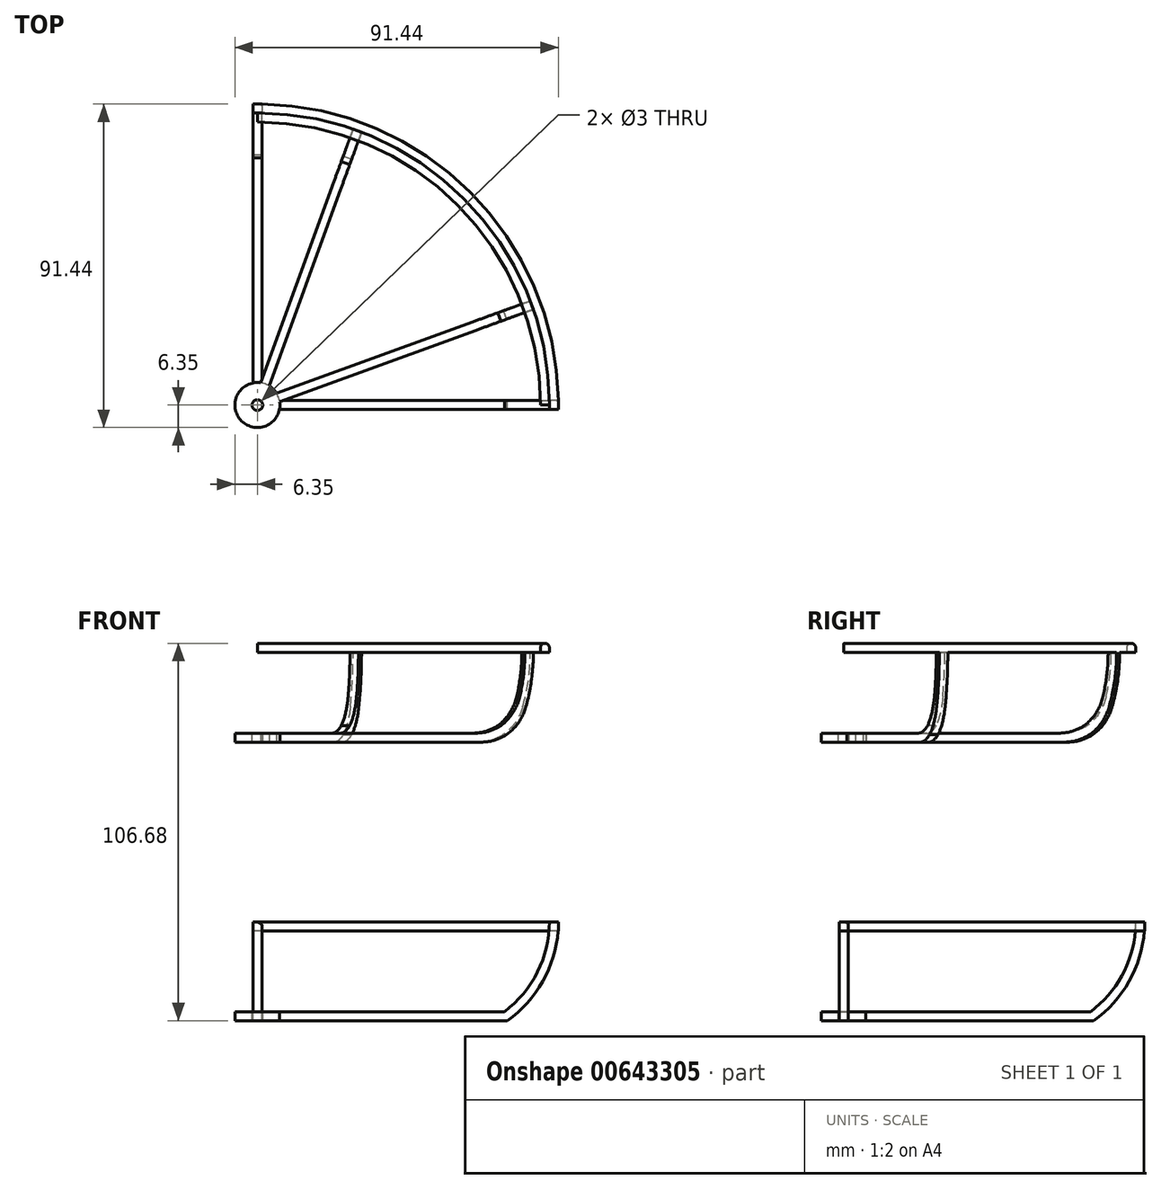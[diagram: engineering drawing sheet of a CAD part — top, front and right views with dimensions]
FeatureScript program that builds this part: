
annotation { "Feature Type Name" : "Feature", "Feature Type Description" : "" }
export const myFeature = defineFeature(function(context is Context, id is Id, definition is map)
    precondition{}
    {
        {
            var Q0;
            Q0=qCreatedBy(makeId("Front.planeOp"),FACE);
            var sketch = newSketch(context, id + "F0", { "sketchPlane" : qUnion([Q0])});
            skLineSegment(sketch, "E0", {"start": v(0, 0) * mm, "end": v(69.85, 0) * mm});
            skLineSegment(sketch, "E1.bottom", {"start": v(69.85, 0) * mm, "end": v(82.55, 0) * mm, "construction": true});
            skLineSegment(sketch, "E1.top", {"start": v(69.85, 25.4) * mm, "end": v(82.55, 25.4) * mm, "construction": true});
            skLineSegment(sketch, "E1.left", {"start": v(69.85, 0) * mm, "end": v(69.85, 25.4) * mm, "construction": true});
            skLineSegment(sketch, "E1.right", {"start": v(82.55, 0) * mm, "end": v(82.55, 25.4) * mm, "construction": true});
            skArc(sketch, "E2", {"start": v(69.85, 0) * mm, "mid": v(79.2, 11.2) * mm, "end": v(82.55, 25.4) * mm});
            skArc(sketch, "E3.0", {"start": v(70.68, -2.54) * mm, "mid": v(81.27, 9.68) * mm, "end": v(85.1, 25.4) * mm});
            skLineSegment(sketch, "E3.1", {"start": v(0, -2.54) * mm, "end": v(70.68, -2.54) * mm});
            skLineSegment(sketch, "E4", {"start": v(82.55, 25.4) * mm, "end": v(85.1, 25.4) * mm});
            skLineSegment(sketch, "E5", {"start": v(0, 0) * mm, "end": v(0, -2.54) * mm});
            skSolve(sketch);
        }
        {
            var Q0;
            Q0 = qSketchRegion(id + "F0", true);
            extrude(context, id + "F1", {"entities" : qUnion([Q0]), "depth" : 2.54 * mm, "offsetDistance" : 25.4 * mm, "symmetric" : true});
        }
        {
            var Q0;
            Q0=qCreatedBy(makeId("Right.planeOp"),FACE);
            var sketch = newSketch(context, id + "F2", { "sketchPlane" : qUnion([Q0])});
            skLineSegment(sketch, "E6", {"start": v(0, 0) * mm, "end": v(69.85, 0) * mm});
            skLineSegment(sketch, "E7.bottom", {"start": v(69.85, 0) * mm, "end": v(82.55, 0) * mm, "construction": true});
            skLineSegment(sketch, "E7.top", {"start": v(69.85, 25.4) * mm, "end": v(82.55, 25.4) * mm, "construction": true});
            skLineSegment(sketch, "E7.left", {"start": v(69.85, 0) * mm, "end": v(69.85, 25.4) * mm, "construction": true});
            skLineSegment(sketch, "E7.right", {"start": v(82.55, 0) * mm, "end": v(82.55, 25.4) * mm, "construction": true});
            skArc(sketch, "E8", {"start": v(69.85, 0) * mm, "mid": v(79.2, 11.2) * mm, "end": v(82.55, 25.4) * mm});
            skArc(sketch, "E9.0", {"start": v(70.68, -2.54) * mm, "mid": v(81.27, 9.68) * mm, "end": v(85.1, 25.4) * mm});
            skLineSegment(sketch, "E9.1", {"start": v(0, -2.54) * mm, "end": v(70.68, -2.54) * mm});
            skLineSegment(sketch, "E10", {"start": v(82.55, 25.4) * mm, "end": v(85.1, 25.4) * mm});
            skLineSegment(sketch, "E11", {"start": v(0, 0) * mm, "end": v(0, -2.54) * mm});
            skSolve(sketch);
        }
        {
            var Q0;
            Q0 = qSketchRegion(id + "F2", true);
            extrude(context, id + "F3", {"entities" : qUnion([Q0]), "operationType" : NewBodyOperationType.ADD, "depth" : 2.54 * mm, "offsetDistance" : 25.4 * mm, "symmetric" : true});
        }
        {
            var Q0;
            Q0=makeQuery(id+"F3.opExtrude","SWEPT_FACE",FACE,{"disambiguationData":[OSD([sQuery(id+"F2.wireOp",EDGE,"E10")])]});
            var sketch = newSketch(context, id + "F4", { "sketchPlane" : qUnion([Q0])});
            skPoint(sketch, "E12", {"position": v(0, 82.55) * mm});
            skLineSegment(sketch, "E13.bottom", {"start": v(0, 82.55) * mm, "end": v(82.55, 82.55) * mm, "construction": true});
            skLineSegment(sketch, "E13.top", {"start": v(0, 0) * mm, "end": v(82.55, 0) * mm, "construction": true});
            skLineSegment(sketch, "E13.left", {"start": v(0, 82.55) * mm, "end": v(0, 0) * mm, "construction": true});
            skLineSegment(sketch, "E13.right", {"start": v(82.55, 82.55) * mm, "end": v(82.55, 0) * mm, "construction": true});
            skArc(sketch, "E14", {"start": v(82.55, 0) * mm, "mid": v(58.37, 58.37) * mm, "end": v(0, 82.55) * mm});
            skArc(sketch, "E15.0", {"start": v(85.1, 0) * mm, "mid": v(60.17, 60.17) * mm, "end": v(0, 85.1) * mm});
            skLineSegment(sketch, "E16", {"start": v(82.55, 0) * mm, "end": v(83.82, 0) * mm, "construction": true});
            skLineSegment(sketch, "E17.bottom", {"start": v(85.1, -1.27) * mm, "end": v(82.55, -1.27) * mm});
            skLineSegment(sketch, "E17.top", {"start": v(85.1, 1.27) * mm, "end": v(82.55, 1.27) * mm});
            skLineSegment(sketch, "E17.left", {"start": v(85.1, -1.27) * mm, "end": v(85.1, 1.27) * mm});
            skLineSegment(sketch, "E17.right", {"start": v(82.55, -1.27) * mm, "end": v(82.55, 1.27) * mm});
            skPoint(sketch, "E17.middle", {"position": v(83.82, 0) * mm});
            skLineSegment(sketch, "E18", {"start": v(0, 82.55) * mm, "end": v(0, 83.82) * mm, "construction": true});
            skLineSegment(sketch, "E19.bottom", {"start": v(1.27, 85.1) * mm, "end": v(-1.27, 85.1) * mm});
            skLineSegment(sketch, "E19.top", {"start": v(1.27, 82.55) * mm, "end": v(-1.27, 82.55) * mm});
            skLineSegment(sketch, "E19.left", {"start": v(1.27, 85.1) * mm, "end": v(1.27, 82.55) * mm});
            skLineSegment(sketch, "E19.right", {"start": v(-1.27, 85.1) * mm, "end": v(-1.27, 82.55) * mm});
            skPoint(sketch, "E19.middle", {"position": v(0, 83.82) * mm});
            skSolve(sketch);
        }
        {
            var Q0;
            Q0 = qSketchRegion(id + "F4", true);
            extrude(context, id + "F5", {"entities" : qUnion([Q0]), "operationType" : NewBodyOperationType.ADD, "oppositeDirection" : true, "depth" : 2.54 * mm, "offsetDistance" : 25.4 * mm});
        }
        {
            var Q0;
            Q0=qCreatedBy(makeId("Top.planeOp"),FACE);
            var sketch = newSketch(context, id + "F6", { "sketchPlane" : qUnion([Q0])});
            skCircle(sketch, "E20", {"center": v(0, 0) * mm, "radius": 6.35 * mm});
            skSolve(sketch);
        }
        {
            var Q0;
            Q0 = qSketchRegion(id + "F6", true);
            extrude(context, id + "F7", {"entities" : qUnion([Q0]), "operationType" : NewBodyOperationType.ADD, "oppositeDirection" : true, "depth" : 2.54 * mm, "offsetDistance" : 25.4 * mm});
        }
        {
            var Q0;
            Q0=qCreatedBy(makeId("Top.planeOp"),FACE);
            var sketch = newSketch(context, id + "F8", { "sketchPlane" : qUnion([Q0])});
            skCircle(sketch, "E21", {"center": v(0, 0) * mm, "radius": 1.5 * mm});
            skSolve(sketch);
        }
        {
            var Q0;
            Q0 = qSketchRegion(id + "F8", true);
            extrude(context, id + "F9", {"entities" : qUnion([Q0]), "operationType" : NewBodyOperationType.REMOVE, "oppositeDirection" : true, "depth" : 2.54 * mm, "offsetDistance" : 25.4 * mm});
        }
        {
            var Q0;
            Q0=makeQuery(id+"F5.boolean.opBoolean","MERGE",FACE,{"derivedFrom":[makeQuery(id+"F1.opExtrude","SWEPT_FACE",FACE,{"disambiguationData":[OSD([sQuery(id+"F0.wireOp",EDGE,"E4")])]}),makeQuery(id+"F3.opExtrude","SWEPT_FACE",FACE,{"disambiguationData":[OSD([sQuery(id+"F2.wireOp",EDGE,"E10")])]}),makeQuery(id+"F5.opExtrude","CAP_FACE",FACE,{"disambiguationData":[OSD([sQuery(id+"F4.wireOp",EDGE,"E14"),sQuery(id+"F4.wireOp",EDGE,"E15.0"),sQuery(id+"F4.wireOp",EDGE,"E17.bottom"),sQuery(id+"F4.wireOp",EDGE,"E17.top"),sQuery(id+"F4.wireOp",EDGE,"E17.left"),sQuery(id+"F4.wireOp",EDGE,"E17.right"),sQuery(id+"F4.wireOp",EDGE,"E19.bottom"),sQuery(id+"F4.wireOp",EDGE,"E19.top"),sQuery(id+"F4.wireOp",EDGE,"E19.left"),sQuery(id+"F4.wireOp",EDGE,"E19.right")])],"isStart":true})]});
            cPlane(context, id + "F10", {"entities" : qUnion([Q0]), "cplaneType" : CPlaneType.OFFSET, "offset" : 50.8 * mm, "width" : 152.4 * mm, "height" : 152.4 * mm});
        }
        {
            var Q0;
            Q0=qCreatedBy(id+"F10.planeOp",FACE);
            var sketch = newSketch(context, id + "F11", { "sketchPlane" : qUnion([Q0])});
            skCircle(sketch, "E22", {"center": v(0, 0) * mm, "radius": 6.35 * mm});
            skLineSegment(sketch, "E23", {"start": v(0, 0) * mm, "end": v(69.85, 0) * mm, "construction": true});
            skLineSegment(sketch, "E24", {"start": v(0, 0) * mm, "end": v(71.6, 26.06) * mm, "construction": true});
            skLineSegment(sketch, "E25", {"start": v(0, 0) * mm, "end": v(26.06, 71.6) * mm, "construction": true});
            skLineSegment(sketch, "E26.0", {"start": v(-2.12, -2.12) * mm, "end": v(72.04, 24.87) * mm});
            skLineSegment(sketch, "E26.1", {"start": v(-2.12, -2.12) * mm, "end": v(24.87, 72.04) * mm});
            skLineSegment(sketch, "E27.0", {"start": v(2.12, 2.12) * mm, "end": v(71.17, 27.26) * mm});
            skLineSegment(sketch, "E27.1", {"start": v(2.12, 2.12) * mm, "end": v(27.26, 71.17) * mm});
            skLineSegment(sketch, "E28", {"start": v(24.87, 72.04) * mm, "end": v(27.26, 71.17) * mm});
            skLineSegment(sketch, "E29", {"start": v(71.17, 27.26) * mm, "end": v(72.04, 24.87) * mm});
            skSolve(sketch);
        }
        {
            var Q0;
            Q0 = qSketchRegion(id + "F11", true);
            extrude(context, id + "F12", {"entities" : qUnion([Q0]), "depth" : 2.54 * mm, "offsetDistance" : 25.4 * mm});
        }
        {
            var Q0;
            Q0=makeQuery(id+"F12.opExtrude","SWEPT_FACE",FACE,{"disambiguationData":[OSD([sQuery(id+"F11.wireOp",EDGE,"E26.0")])]});
            var sketch = newSketch(context, id + "F13", { "sketchPlane" : qUnion([Q0])});
            skLineSegment(sketch, "E30.bottom", {"start": v(76.2, 76.2) * mm, "end": v(82.55, 76.2) * mm, "construction": true});
            skLineSegment(sketch, "E30.top", {"start": v(76.2, 101.6) * mm, "end": v(82.55, 101.6) * mm, "construction": true});
            skLineSegment(sketch, "E30.left", {"start": v(76.2, 76.2) * mm, "end": v(76.2, 101.6) * mm, "construction": true});
            skLineSegment(sketch, "E30.right", {"start": v(82.55, 76.2) * mm, "end": v(82.55, 101.6) * mm, "construction": true});
            skArc(sketch, "E31", {"start": v(76.2, 76.2) * mm, "mid": v(80.94, 88.5) * mm, "end": v(82.55, 101.6) * mm});
            skArc(sketch, "E32.0", {"start": v(73.96, 77.4) * mm, "mid": v(78.47, 89.13) * mm, "end": v(80.01, 101.6) * mm});
            skLineSegment(sketch, "E33", {"start": v(73.96, 77.4) * mm, "end": v(76.2, 76.2) * mm});
            skLineSegment(sketch, "E34", {"start": v(82.55, 101.6) * mm, "end": v(80.01, 101.6) * mm});
            skSolve(sketch);
        }
        {
            var Q0;
            Q0 = qSketchRegion(id + "F13", true);
            extrude(context, id + "F14", {"entities" : qUnion([Q0]), "operationType" : NewBodyOperationType.ADD, "oppositeDirection" : true, "depth" : 2.54 * mm, "offsetDistance" : 25.4 * mm});
        }
        {
            var Q0;
            Q0=makeQuery(id+"F12.opExtrude","SWEPT_FACE",FACE,{"disambiguationData":[OSD([sQuery(id+"F11.wireOp",EDGE,"E27.1")])]});
            var sketch = newSketch(context, id + "F15", { "sketchPlane" : qUnion([Q0])});
            skLineSegment(sketch, "E35.bottom", {"start": v(76.2, 76.2) * mm, "end": v(82.55, 76.2) * mm, "construction": true});
            skLineSegment(sketch, "E35.top", {"start": v(76.2, 101.6) * mm, "end": v(82.55, 101.6) * mm, "construction": true});
            skLineSegment(sketch, "E35.left", {"start": v(76.2, 76.2) * mm, "end": v(76.2, 101.6) * mm, "construction": true});
            skLineSegment(sketch, "E35.right", {"start": v(82.55, 76.2) * mm, "end": v(82.55, 101.6) * mm, "construction": true});
            skArc(sketch, "E36", {"start": v(76.2, 76.2) * mm, "mid": v(80.94, 88.5) * mm, "end": v(82.55, 101.6) * mm});
            skArc(sketch, "E37.0", {"start": v(73.96, 77.4) * mm, "mid": v(78.47, 89.13) * mm, "end": v(80.01, 101.6) * mm});
            skLineSegment(sketch, "E38", {"start": v(73.96, 77.4) * mm, "end": v(76.2, 76.2) * mm});
            skLineSegment(sketch, "E39", {"start": v(82.55, 101.6) * mm, "end": v(80.01, 101.6) * mm});
            skSolve(sketch);
        }
        {
            var Q0;
            Q0 = qSketchRegion(id + "F15", true);
            extrude(context, id + "F16", {"entities" : qUnion([Q0]), "operationType" : NewBodyOperationType.ADD, "oppositeDirection" : true, "depth" : 2.54 * mm, "offsetDistance" : 25.4 * mm});
        }
        {
            var Q0;
            Q0=makeQuery(id+"F16.opExtrude","SWEPT_FACE",FACE,{"disambiguationData":[OSD([sQuery(id+"F15.wireOp",EDGE,"E39")])]});
            var sketch = newSketch(context, id + "F17", { "sketchPlane" : qUnion([Q0])});
            skLineSegment(sketch, "E40", {"start": v(0, 0) * mm, "end": v(0, 80.01) * mm, "construction": true});
            skLineSegment(sketch, "E41", {"start": v(0, 0) * mm, "end": v(80.01, 0) * mm, "construction": true});
            skArc(sketch, "E42", {"start": v(80.01, 0) * mm, "mid": v(56.58, 56.58) * mm, "end": v(0, 80.01) * mm});
            skArc(sketch, "E43.0", {"start": v(82.55, 0) * mm, "mid": v(58.37, 58.37) * mm, "end": v(0, 82.55) * mm});
            skLineSegment(sketch, "E44", {"start": v(0, 80.01) * mm, "end": v(0, 82.55) * mm});
            skLineSegment(sketch, "E45", {"start": v(80.01, 0) * mm, "end": v(82.55, 0) * mm});
            skSolve(sketch);
        }
        {
            var Q0;
            Q0 = qSketchRegion(id + "F17", true);
            extrude(context, id + "F18", {"entities" : qUnion([Q0]), "operationType" : NewBodyOperationType.ADD, "depth" : 2.54 * mm, "offsetDistance" : 25.4 * mm});
        }
        {
            var Q0;
            Q0=makeQuery(id+"F12.opExtrude","CAP_FACE",FACE,{"disambiguationData":[OSD([sQuery(id+"F11.wireOp",EDGE,"E22"),sQuery(id+"F11.wireOp",EDGE,"E26.0"),sQuery(id+"F11.wireOp",EDGE,"E26.1"),sQuery(id+"F11.wireOp",EDGE,"E27.0"),sQuery(id+"F11.wireOp",EDGE,"E27.1"),sQuery(id+"F11.wireOp",EDGE,"E28"),sQuery(id+"F11.wireOp",EDGE,"E29")])],"isStart":false});
            var sketch = newSketch(context, id + "F19", { "sketchPlane" : qUnion([Q0])});
            skCircle(sketch, "E46", {"center": v(0, 0) * mm, "radius": 1.5 * mm});
            skSolve(sketch);
        }
        {
            var Q0;
            Q0 = qSketchRegion(id + "F19", true);
            extrude(context, id + "F20", {"entities" : qUnion([Q0]), "operationType" : NewBodyOperationType.REMOVE, "oppositeDirection" : true, "depth" : 2.54 * mm, "offsetDistance" : 25.4 * mm});
        }
        {
            var Q0;
            Q0=makeQuery(id+"F14.boolean.opBoolean","INTERSECT",EDGE,{"derivedFrom":[makeQuery(id+"F12.opExtrude","CAP_FACE",FACE,{"disambiguationData":[OSD([sQuery(id+"F11.wireOp",EDGE,"E22"),sQuery(id+"F11.wireOp",EDGE,"E26.0"),sQuery(id+"F11.wireOp",EDGE,"E26.1"),sQuery(id+"F11.wireOp",EDGE,"E27.0"),sQuery(id+"F11.wireOp",EDGE,"E27.1"),sQuery(id+"F11.wireOp",EDGE,"E28"),sQuery(id+"F11.wireOp",EDGE,"E29")])],"isStart":false}),makeQuery(id+"F14.opExtrude","SWEPT_FACE",FACE,{"disambiguationData":[OSD([sQuery(id+"F13.wireOp",EDGE,"E32.0")])]})]});
            var Q1;
            Q1=makeQuery(id+"F16.boolean.opBoolean","INTERSECT",EDGE,{"derivedFrom":[makeQuery(id+"F12.opExtrude","CAP_FACE",FACE,{"disambiguationData":[OSD([sQuery(id+"F11.wireOp",EDGE,"E22"),sQuery(id+"F11.wireOp",EDGE,"E26.0"),sQuery(id+"F11.wireOp",EDGE,"E26.1"),sQuery(id+"F11.wireOp",EDGE,"E27.0"),sQuery(id+"F11.wireOp",EDGE,"E27.1"),sQuery(id+"F11.wireOp",EDGE,"E28"),sQuery(id+"F11.wireOp",EDGE,"E29")])],"isStart":false}),makeQuery(id+"F16.opExtrude","SWEPT_FACE",FACE,{"disambiguationData":[OSD([sQuery(id+"F15.wireOp",EDGE,"E37.0")])]})]});
            var Q2;
            {var subQ0=sQuery(id+"F11.wireOp",EDGE,"E28");Q2=makeQuery(id+"F16.boolean.opBoolean","MERGE",EDGE,{"derivedFrom":[makeQuery(id+"F12.opExtrude","CAP_EDGE",EDGE,{"disambiguationData":[OSD([subQ0])],"isStart":true}),makeQuery(id+"F16.opExtrude","SWEPT_EDGE",EDGE,{"disambiguationData":[OSD([sQuery(id+"F11.wireOp",EDGE,"E27.1"),subQ0,sQuery(id+"F15.wireOp",EDGE,"E36"),sQuery(id+"F15.wireOp",EDGE,"E38")])]})]});}
            var Q3;
            {var subQ0=sQuery(id+"F11.wireOp",EDGE,"E29");Q3=makeQuery(id+"F14.boolean.opBoolean","MERGE",EDGE,{"derivedFrom":[makeQuery(id+"F12.opExtrude","CAP_EDGE",EDGE,{"disambiguationData":[OSD([subQ0])],"isStart":true}),makeQuery(id+"F14.opExtrude","SWEPT_EDGE",EDGE,{"disambiguationData":[OSD([sQuery(id+"F11.wireOp",EDGE,"E26.0"),subQ0,sQuery(id+"F13.wireOp",EDGE,"E31"),sQuery(id+"F13.wireOp",EDGE,"E33")])]})]});}
            chamfer(context, id + "F21", {"entities" : qUnion([Q0, Q1, Q2, Q3]), "width" : 5.08 * mm, "tangentPropagation" : true});
        }
        {
            var Q0;
            {var subQ0=sQuery(id+"F13.wireOp",EDGE,"E31");var subQ1=sQuery(id+"F11.wireOp",EDGE,"E29");Q0=makeQuery(id+"F21.opChamfer","BLEND_EDGE",EDGE,{"blendedFrom":[makeQuery(id+"F14.boolean.opBoolean","MERGE",EDGE,{"derivedFrom":[makeQuery(id+"F12.opExtrude","CAP_EDGE",EDGE,{"disambiguationData":[OSD([subQ1])],"isStart":true}),makeQuery(id+"F14.opExtrude","SWEPT_EDGE",EDGE,{"disambiguationData":[OSD([sQuery(id+"F11.wireOp",EDGE,"E26.0"),subQ1,subQ0,sQuery(id+"F13.wireOp",EDGE,"E33")])]})]}),makeQuery(id+"F14.opExtrude","SWEPT_FACE",FACE,{"disambiguationData":[OSD([subQ0])]})],"blendedInto":[makeQuery(id+"F14.opExtrude","SWEPT_FACE",FACE,{"disambiguationData":[OSD([subQ0])]})]});}
            var Q1;
            {var subQ0=sQuery(id+"F11.wireOp",EDGE,"E29");var subQ1=sQuery(id+"F11.wireOp",EDGE,"E26.0");Q1=makeQuery(id+"F21.opChamfer","BLEND_EDGE",EDGE,{"blendedFrom":[makeQuery(id+"F14.boolean.opBoolean","MERGE",EDGE,{"derivedFrom":[makeQuery(id+"F12.opExtrude","CAP_EDGE",EDGE,{"disambiguationData":[OSD([subQ0])],"isStart":true}),makeQuery(id+"F14.opExtrude","SWEPT_EDGE",EDGE,{"disambiguationData":[OSD([subQ1,subQ0,sQuery(id+"F13.wireOp",EDGE,"E31"),sQuery(id+"F13.wireOp",EDGE,"E33")])]})]}),makeQuery(id+"F12.opExtrude","CAP_FACE",FACE,{"disambiguationData":[OSD([sQuery(id+"F11.wireOp",EDGE,"E22"),subQ1,sQuery(id+"F11.wireOp",EDGE,"E26.1"),sQuery(id+"F11.wireOp",EDGE,"E27.0"),sQuery(id+"F11.wireOp",EDGE,"E27.1"),sQuery(id+"F11.wireOp",EDGE,"E28"),subQ0])],"isStart":true})],"blendedInto":[makeQuery(id+"F12.opExtrude","CAP_FACE",FACE,{"disambiguationData":[OSD([sQuery(id+"F11.wireOp",EDGE,"E22"),subQ1,sQuery(id+"F11.wireOp",EDGE,"E26.1"),sQuery(id+"F11.wireOp",EDGE,"E27.0"),sQuery(id+"F11.wireOp",EDGE,"E27.1"),sQuery(id+"F11.wireOp",EDGE,"E28"),subQ0])],"isStart":true})]});}
            var Q2;
            {var subQ0=makeQuery(id+"F14.opExtrude","SWEPT_FACE",FACE,{"disambiguationData":[OSD([sQuery(id+"F13.wireOp",EDGE,"E32.0")])]});Q2=makeQuery(id+"F21.opChamfer","BLEND_EDGE",EDGE,{"blendedFrom":[makeQuery(id+"F14.boolean.opBoolean","INTERSECT",EDGE,{"derivedFrom":[makeQuery(id+"F12.opExtrude","CAP_FACE",FACE,{"disambiguationData":[OSD([sQuery(id+"F11.wireOp",EDGE,"E22"),sQuery(id+"F11.wireOp",EDGE,"E26.0"),sQuery(id+"F11.wireOp",EDGE,"E26.1"),sQuery(id+"F11.wireOp",EDGE,"E27.0"),sQuery(id+"F11.wireOp",EDGE,"E27.1"),sQuery(id+"F11.wireOp",EDGE,"E28"),sQuery(id+"F11.wireOp",EDGE,"E29")])],"isStart":false}),subQ0]}),subQ0],"blendedInto":[subQ0]});}
            var Q3;
            {var subQ0=makeQuery(id+"F12.opExtrude","CAP_FACE",FACE,{"disambiguationData":[OSD([sQuery(id+"F11.wireOp",EDGE,"E22"),sQuery(id+"F11.wireOp",EDGE,"E26.0"),sQuery(id+"F11.wireOp",EDGE,"E26.1"),sQuery(id+"F11.wireOp",EDGE,"E27.0"),sQuery(id+"F11.wireOp",EDGE,"E27.1"),sQuery(id+"F11.wireOp",EDGE,"E28"),sQuery(id+"F11.wireOp",EDGE,"E29")])],"isStart":false});Q3=makeQuery(id+"F21.opChamfer","BLEND_EDGE",EDGE,{"blendedFrom":[makeQuery(id+"F14.boolean.opBoolean","INTERSECT",EDGE,{"derivedFrom":[subQ0,makeQuery(id+"F14.opExtrude","SWEPT_FACE",FACE,{"disambiguationData":[OSD([sQuery(id+"F13.wireOp",EDGE,"E32.0")])]})]}),subQ0],"blendedInto":[subQ0]});}
            var Q4;
            {var subQ0=makeQuery(id+"F12.opExtrude","CAP_FACE",FACE,{"disambiguationData":[OSD([sQuery(id+"F11.wireOp",EDGE,"E22"),sQuery(id+"F11.wireOp",EDGE,"E26.0"),sQuery(id+"F11.wireOp",EDGE,"E26.1"),sQuery(id+"F11.wireOp",EDGE,"E27.0"),sQuery(id+"F11.wireOp",EDGE,"E27.1"),sQuery(id+"F11.wireOp",EDGE,"E28"),sQuery(id+"F11.wireOp",EDGE,"E29")])],"isStart":false});Q4=makeQuery(id+"F21.opChamfer","BLEND_EDGE",EDGE,{"blendedFrom":[makeQuery(id+"F16.boolean.opBoolean","INTERSECT",EDGE,{"derivedFrom":[subQ0,makeQuery(id+"F16.opExtrude","SWEPT_FACE",FACE,{"disambiguationData":[OSD([sQuery(id+"F15.wireOp",EDGE,"E37.0")])]})]}),subQ0],"blendedInto":[subQ0]});}
            var Q5;
            {var subQ0=makeQuery(id+"F16.opExtrude","SWEPT_FACE",FACE,{"disambiguationData":[OSD([sQuery(id+"F15.wireOp",EDGE,"E37.0")])]});Q5=makeQuery(id+"F21.opChamfer","BLEND_EDGE",EDGE,{"blendedFrom":[makeQuery(id+"F16.boolean.opBoolean","INTERSECT",EDGE,{"derivedFrom":[makeQuery(id+"F12.opExtrude","CAP_FACE",FACE,{"disambiguationData":[OSD([sQuery(id+"F11.wireOp",EDGE,"E22"),sQuery(id+"F11.wireOp",EDGE,"E26.0"),sQuery(id+"F11.wireOp",EDGE,"E26.1"),sQuery(id+"F11.wireOp",EDGE,"E27.0"),sQuery(id+"F11.wireOp",EDGE,"E27.1"),sQuery(id+"F11.wireOp",EDGE,"E28"),sQuery(id+"F11.wireOp",EDGE,"E29")])],"isStart":false}),subQ0]}),subQ0],"blendedInto":[subQ0]});}
            var Q6;
            {var subQ0=sQuery(id+"F15.wireOp",EDGE,"E36");var subQ1=sQuery(id+"F11.wireOp",EDGE,"E28");Q6=makeQuery(id+"F21.opChamfer","BLEND_EDGE",EDGE,{"blendedFrom":[makeQuery(id+"F16.boolean.opBoolean","MERGE",EDGE,{"derivedFrom":[makeQuery(id+"F12.opExtrude","CAP_EDGE",EDGE,{"disambiguationData":[OSD([subQ1])],"isStart":true}),makeQuery(id+"F16.opExtrude","SWEPT_EDGE",EDGE,{"disambiguationData":[OSD([sQuery(id+"F11.wireOp",EDGE,"E27.1"),subQ1,subQ0,sQuery(id+"F15.wireOp",EDGE,"E38")])]})]}),makeQuery(id+"F16.opExtrude","SWEPT_FACE",FACE,{"disambiguationData":[OSD([subQ0])]})],"blendedInto":[makeQuery(id+"F16.opExtrude","SWEPT_FACE",FACE,{"disambiguationData":[OSD([subQ0])]})]});}
            var Q7;
            {var subQ0=sQuery(id+"F11.wireOp",EDGE,"E28");var subQ1=sQuery(id+"F11.wireOp",EDGE,"E27.1");Q7=makeQuery(id+"F21.opChamfer","BLEND_EDGE",EDGE,{"blendedFrom":[makeQuery(id+"F16.boolean.opBoolean","MERGE",EDGE,{"derivedFrom":[makeQuery(id+"F12.opExtrude","CAP_EDGE",EDGE,{"disambiguationData":[OSD([subQ0])],"isStart":true}),makeQuery(id+"F16.opExtrude","SWEPT_EDGE",EDGE,{"disambiguationData":[OSD([subQ1,subQ0,sQuery(id+"F15.wireOp",EDGE,"E36"),sQuery(id+"F15.wireOp",EDGE,"E38")])]})]}),makeQuery(id+"F12.opExtrude","CAP_FACE",FACE,{"disambiguationData":[OSD([sQuery(id+"F11.wireOp",EDGE,"E22"),sQuery(id+"F11.wireOp",EDGE,"E26.0"),sQuery(id+"F11.wireOp",EDGE,"E26.1"),sQuery(id+"F11.wireOp",EDGE,"E27.0"),subQ1,subQ0,sQuery(id+"F11.wireOp",EDGE,"E29")])],"isStart":true})],"blendedInto":[makeQuery(id+"F12.opExtrude","CAP_FACE",FACE,{"disambiguationData":[OSD([sQuery(id+"F11.wireOp",EDGE,"E22"),sQuery(id+"F11.wireOp",EDGE,"E26.0"),sQuery(id+"F11.wireOp",EDGE,"E26.1"),sQuery(id+"F11.wireOp",EDGE,"E27.0"),subQ1,subQ0,sQuery(id+"F11.wireOp",EDGE,"E29")])],"isStart":true})]});}
            fillet(context, id + "F22", {"entities" : qUnion([Q0, Q1, Q2, Q3, Q4, Q5, Q6, Q7]), "radius" : 14.22 * mm, "tangentPropagation" : true, "allowEdgeOverflow" : false});
        }
        {
            var Q0;
            Q0=makeQuery(id+"F18.opExtrude","CAP_EDGE",EDGE,{"disambiguationData":[OSD([sQuery(id+"F17.wireOp",EDGE,"E42")])],"isStart":false});
            var Q1;
            Q1=makeQuery(id+"F18.opExtrude","CAP_EDGE",EDGE,{"disambiguationData":[OSD([sQuery(id+"F17.wireOp",EDGE,"E43.0")])],"isStart":false});
            fillet(context, id + "F23", {"entities" : qUnion([Q0, Q1]), "radius" : 1.27 * mm, "tangentPropagation" : true, "allowEdgeOverflow" : false});
        }
    });
